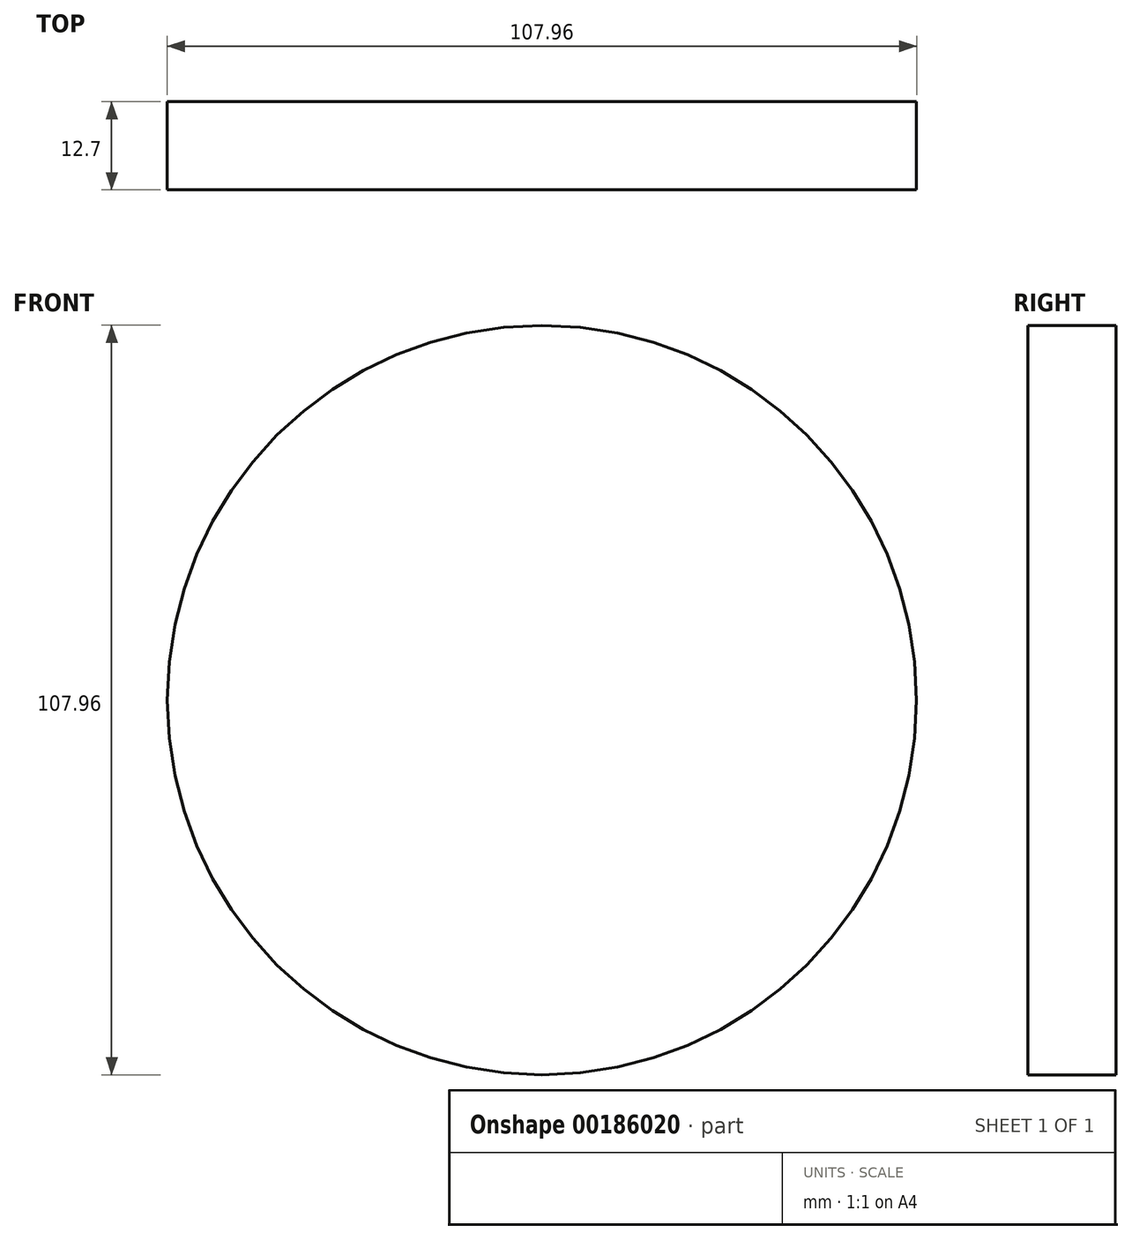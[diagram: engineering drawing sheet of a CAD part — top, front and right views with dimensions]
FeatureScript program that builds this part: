
annotation { "Feature Type Name" : "Feature", "Feature Type Description" : "" }
export const myFeature = defineFeature(function(context is Context, id is Id, definition is map)
    precondition{}
    {
        {
            var Q0;
            Q0=qCreatedBy(makeId("Front.planeOp"),FACE);
            var sketch = newSketch(context, id + "F0", { "sketchPlane" : qUnion([Q0])});
            skCircle(sketch, "E0", {"center": v(0, 0) * mm, "radius": 53.98 * mm});
            skSolve(sketch);
        }
        {
            var Q0;
            Q0=makeQuery(id+"F0.imprint","IMPRINT",FACE,{"disambiguationData":[TD([[makeQuery(id+"F0.imprint","IMPRINT",EDGE,{"derivedFrom":sQuery(id+"F0.wireOp",EDGE,"E0")}),1.0]])]});
            extrude(context, id + "F1", {"entities" : qUnion([Q0]), "depth" : 12.7 * mm});
        }
    });
